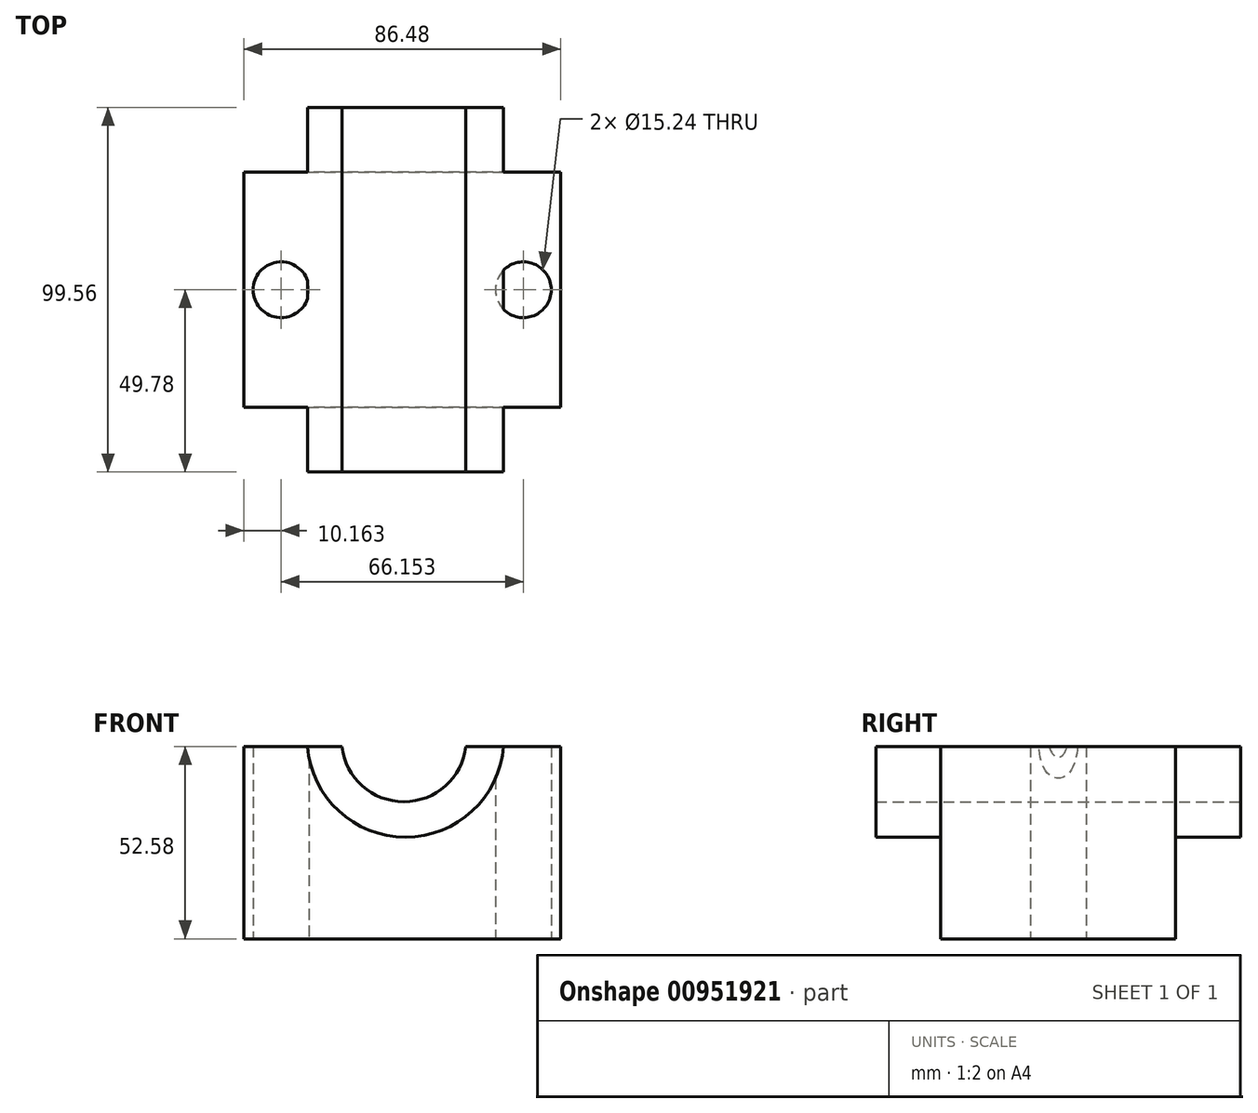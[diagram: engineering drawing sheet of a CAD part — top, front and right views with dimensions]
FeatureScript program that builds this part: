
annotation { "Feature Type Name" : "Feature", "Feature Type Description" : "" }
export const myFeature = defineFeature(function(context is Context, id is Id, definition is map)
    precondition{}
    {
        {
            var Q0;
            Q0=qCreatedBy(makeId("Top.planeOp"),FACE);
            var sketch = newSketch(context, id + "F0", { "sketchPlane" : qUnion([Q0])});
            skLineSegment(sketch, "E0.bottom", {"start": v(43.24, -32.1) * mm, "end": v(-43.24, -32.1) * mm});
            skLineSegment(sketch, "E0.top", {"start": v(43.24, 32.1) * mm, "end": v(-43.24, 32.1) * mm});
            skLineSegment(sketch, "E0.left", {"start": v(43.24, -32.1) * mm, "end": v(43.24, 32.1) * mm});
            skLineSegment(sketch, "E0.right", {"start": v(-43.24, -32.1) * mm, "end": v(-43.24, 32.1) * mm});
            skPoint(sketch, "E0.middle", {"position": v(0, 0) * mm});
            skSolve(sketch);
        }
        {
            var Q0;
            Q0=makeQuery(id+"F0.imprint","IMPRINT",FACE,{"disambiguationData":[TD([[makeQuery(id+"F0.imprint","IMPRINT",EDGE,{"derivedFrom":sQuery(id+"F0.wireOp",EDGE,"E0.bottom")}),-1.0]])]});
            extrude(context, id + "F1", {"entities" : qUnion([Q0]), "depth" : 52.58 * mm, "offsetDistance" : 25.4 * mm});
        }
        {
            var Q0;
            Q0=qCreatedBy(makeId("Top.planeOp"),FACE);
            var sketch = newSketch(context, id + "F2", { "sketchPlane" : qUnion([Q0])});
            skCircle(sketch, "E1", {"center": v(33.08, 0) * mm, "radius": 7.62 * mm});
            skCircle(sketch, "E2", {"center": v(-33.08, 0) * mm, "radius": 7.62 * mm});
            skSolve(sketch);
        }
        {
            var Q0;
            Q0 = qSketchRegion(id + "F2", true);
            extrude(context, id + "F3", {"entities" : qUnion([Q0]), "operationType" : NewBodyOperationType.REMOVE, "depth" : 180.34 * mm, "offsetDistance" : 25.4 * mm});
        }
        {
            var Q0;
            Q0=qCreatedBy(makeId("Front.planeOp"),FACE);
            var sketch = newSketch(context, id + "F4", { "sketchPlane" : qUnion([Q0])});
            skArc(sketch, "E3", {"start": v(-16.5, 52.58) * mm, "mid": v(0.45, 37.46) * mm, "end": v(17.38, 52.58) * mm});
            skArc(sketch, "E4", {"start": v(-25.85, 52.58) * mm, "mid": v(0.9, 27.8) * mm, "end": v(27.64, 52.58) * mm});
            skLineSegment(sketch, "E5", {"start": v(-25.85, 52.58) * mm, "end": v(-16.5, 52.58) * mm});
            skLineSegment(sketch, "E6", {"start": v(17.38, 52.58) * mm, "end": v(27.64, 52.58) * mm});
            skSolve(sketch);
        }
        {
            var Q0;
            Q0 = qSketchRegion(id + "F4", true);
            extrude(context, id + "F5", {"entities" : qUnion([Q0]), "operationType" : NewBodyOperationType.ADD, "depth" : 99.57 * mm, "offsetDistance" : 25.4 * mm, "symmetric" : true});
        }
        {
            var Q0;
            Q0=qCreatedBy(makeId("Front.planeOp"),FACE);
            var sketch = newSketch(context, id + "F6", { "sketchPlane" : qUnion([Q0])});
            skArc(sketch, "E7", {"start": v(-16.24, 52.86) * mm, "mid": v(0.71, 37.56) * mm, "end": v(17.67, 52.86) * mm});
            skSolve(sketch);
        }
        {
            var Q0;
            Q0 = qSketchRegion(id + "F6", true);
            var Q1;
            {var subQ0=sQuery(id+"F0.wireOp",EDGE,"E0.top");Q1=makeQuery(id+"F5.boolean.opBoolean","SPLIT",FACE,{"disambiguationData":[TD([makeQuery(id+"F5.opExtrude","SWEPT_FACE",FACE,{"disambiguationData":[OSD([sQuery(id+"F4.wireOp",EDGE,"E3")])]})])],"derivedFrom":makeQuery(id+"F1.opExtrude","SWEPT_FACE",FACE,{"disambiguationData":[OSD([subQ0])]})});}
            extrude(context, id + "F7", {"entities" : qUnion([Q0, Q1]), "operationType" : NewBodyOperationType.REMOVE, "oppositeDirection" : true, "depth" : 69.34 * mm, "offsetDistance" : 25.4 * mm});
        }
    });
